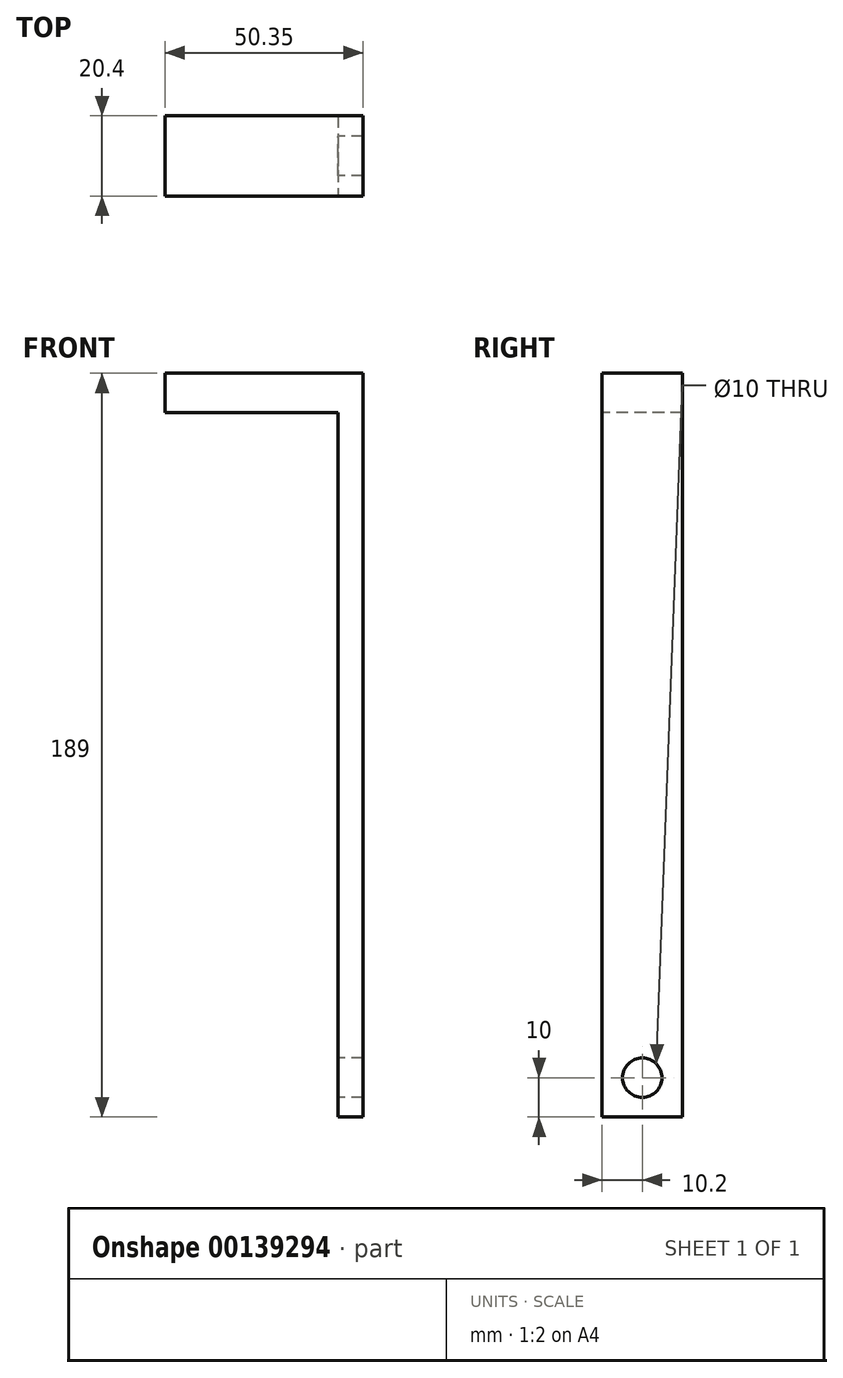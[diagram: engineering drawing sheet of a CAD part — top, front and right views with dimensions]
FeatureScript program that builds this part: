
annotation { "Feature Type Name" : "Feature", "Feature Type Description" : "" }
export const myFeature = defineFeature(function(context is Context, id is Id, definition is map)
    precondition{}
    {
        {
            var Q0;
            Q0=qCreatedBy(makeId("Top.planeOp"),FACE);
            var sketch = newSketch(context, id + "F0", { "sketchPlane" : qUnion([Q0])});
            skLineSegment(sketch, "E0", {"start": v(0, 0) * mm, "end": v(6.35, 0) * mm});
            skLineSegment(sketch, "E1", {"start": v(0, 0) * mm, "end": v(0, 20.4) * mm});
            skLineSegment(sketch, "E2", {"start": v(0, 20.4) * mm, "end": v(6.35, 20.4) * mm});
            skLineSegment(sketch, "E3", {"start": v(6.35, 20.4) * mm, "end": v(6.35, 0) * mm});
            skSolve(sketch);
        }
        {
            var Q0;
            Q0=makeQuery(id+"F0.imprint","IMPRINT",FACE,{"disambiguationData":[TD([[makeQuery(id+"F0.imprint","IMPRINT",EDGE,{"derivedFrom":sQuery(id+"F0.wireOp",EDGE,"E0")}),1.0]])]});
            extrude(context, id + "F1", {"entities" : qUnion([Q0]), "depth" : 189 * mm});
        }
        {
            var Q0;
            Q0=makeQuery(id+"F1.opExtrude","SWEPT_FACE",FACE,{"disambiguationData":[OSD([sQuery(id+"F0.wireOp",EDGE,"E1")])]});
            var sketch = newSketch(context, id + "F2", { "sketchPlane" : qUnion([Q0])});
            skCircle(sketch, "E4", {"center": v(-10.2, 10) * mm, "radius": 5 * mm});
            skPoint(sketch, "E5.start.orphan", {"position": v(-10.2, 0) * mm});
            skSolve(sketch);
        }
        {
            var Q0;
            Q0=makeQuery(id+"F2.imprint","IMPRINT",FACE,{"disambiguationData":[TD([[makeQuery(id+"F2.imprint","IMPRINT",EDGE,{"derivedFrom":sQuery(id+"F2.wireOp",EDGE,"E4")}),1.0]])]});
            var Q1;
            Q1=makeQuery(id+"F1.opExtrude","SWEPT_FACE",FACE,{"disambiguationData":[OSD([sQuery(id+"F0.wireOp",EDGE,"E3")])]});
            extrude(context, id + "F3", {"entities" : qUnion([Q0]), "operationType" : NewBodyOperationType.REMOVE, "endBound" : BoundingType.UP_TO_SURFACE, "oppositeDirection" : true, "endBoundEntityFace" : qUnion([Q1]), "depth" : 25 * mm});
        }
        {
            var Q0;
            Q0=makeQuery(id+"F1.opExtrude","SWEPT_FACE",FACE,{"disambiguationData":[OSD([sQuery(id+"F0.wireOp",EDGE,"E1")])]});
            var sketch = newSketch(context, id + "F4", { "sketchPlane" : qUnion([Q0])});
            skLineSegment(sketch, "E6", {"start": v(-20.4, 189) * mm, "end": v(-20.4, 179) * mm});
            skLineSegment(sketch, "E7", {"start": v(-20.4, 179) * mm, "end": v(0, 179) * mm});
            skLineSegment(sketch, "E8", {"start": v(0, 179) * mm, "end": v(0, 189) * mm});
            skLineSegment(sketch, "E9", {"start": v(0, 189) * mm, "end": v(-20.4, 189) * mm});
            skSolve(sketch);
        }
        {
            var Q0;
            Q0=makeQuery(id+"F4.imprint","IMPRINT",FACE,{"disambiguationData":[TD([[makeQuery(id+"F4.imprint","IMPRINT",EDGE,{"derivedFrom":sQuery(id+"F4.wireOp",EDGE,"E6")}),1.0]])]});
            extrude(context, id + "F5", {"entities" : qUnion([Q0]), "operationType" : NewBodyOperationType.ADD, "depth" : 44 * mm});
        }
    });
